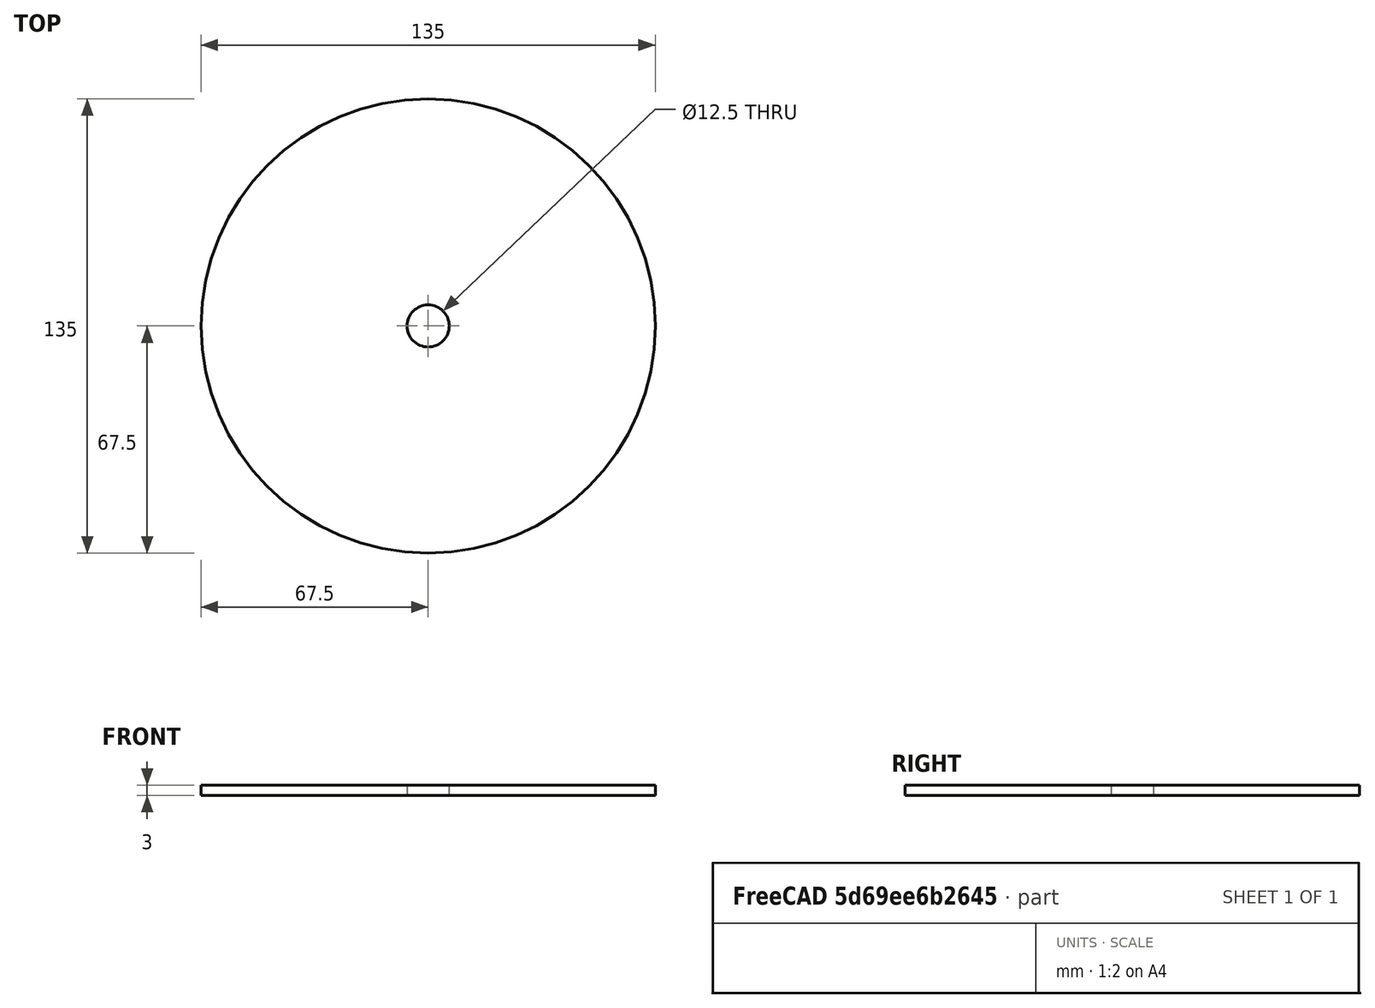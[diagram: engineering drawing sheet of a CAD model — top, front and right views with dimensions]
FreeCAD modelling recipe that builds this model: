
FCSTD DOCUMENT  (FreeCAD 0.19R24291 (Git))
Label: leg_base
License: All rights reserved
LicenseURL: http://en.wikipedia.org/wiki/All_rights_reserved
objects: Sketcher::SketchObject×1, PartDesign::Pad×1, PartDesign::Body×1
note: 4 computed .brp shape members not serialized (recipe doc carries the construction recipe); baked Part::Feature solids carry a one-line shape summary decoded from their .brp

FEATURE [Sketcher::SketchObject] Sketch
  FullyConstrained = true
  MapMode = 5
  Support = -> [XY_Plane]
  sketch-geometry (2):
    g0: Circle CenterX=0 CenterY=0 CenterZ=0 NormalX=0 NormalY=0 NormalZ=1 AngleXU=0 Radius=67.5
    g1: Circle CenterX=0 CenterY=0 CenterZ=0 NormalX=0 NormalY=0 NormalZ=1 AngleXU=0 Radius=6.25
  constraints (4):
    c: Coincident(g0,g-1)
    c: Coincident(g1,g0)
    c: Diameter(g0) = 135
    c: Diameter(g1) = 12.5
FEATURE [PartDesign::Pad] Pad
  Direction = (1,1,1)
  Length = 3
  Length2 = 100
  Profile = -> Sketch
  Type = 0
FEATURE [PartDesign::Body] Body
  Group = -> [Sketch,Pad]
  Origin = -> Origin
  Tip = -> Pad
